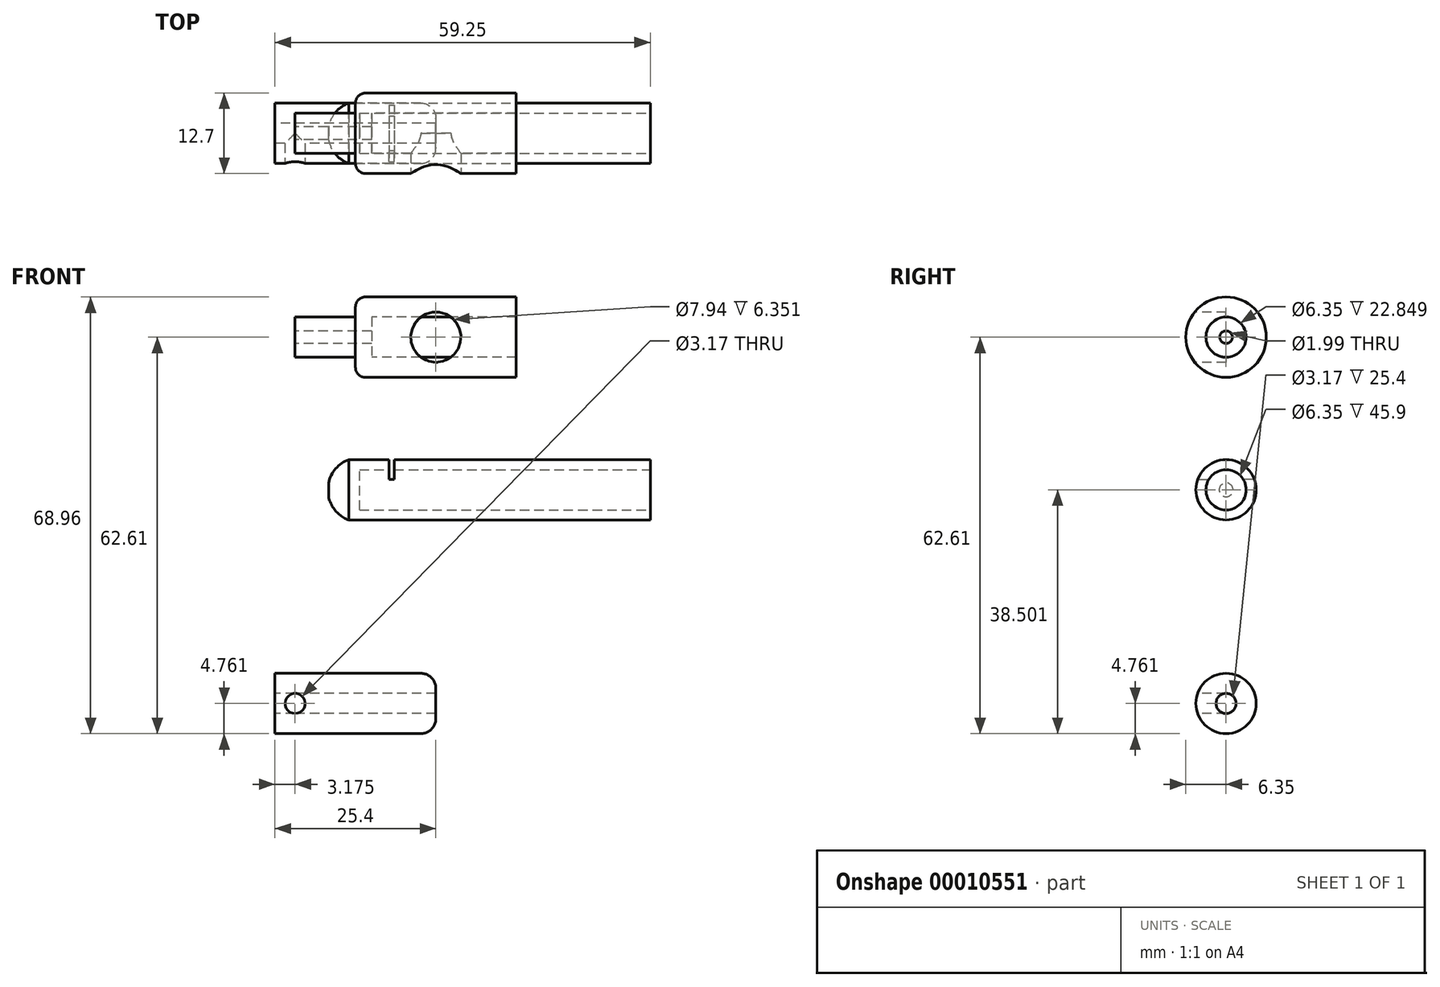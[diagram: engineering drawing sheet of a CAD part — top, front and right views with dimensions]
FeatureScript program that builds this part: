
annotation { "Feature Type Name" : "Feature", "Feature Type Description" : "" }
export const myFeature = defineFeature(function(context is Context, id is Id, definition is map)
    precondition{}
    {
        {
            var Q0;
            Q0=qCreatedBy(makeId("Front.planeOp"),FACE);
            var sketch = newSketch(context, id + "F0", { "sketchPlane" : qUnion([Q0])});
            skLineSegment(sketch, "E0.rect.bottom", {"start": v(12.7, -6.35) * mm, "end": v(-12.7, -6.35) * mm});
            skLineSegment(sketch, "E0.rect.top", {"start": v(12.7, 6.35) * mm, "end": v(-12.7, 6.35) * mm});
            skLineSegment(sketch, "E0.rect.left", {"start": v(12.7, -6.35) * mm, "end": v(12.7, 6.35) * mm});
            skLineSegment(sketch, "E0.rect.right", {"start": v(-12.7, -6.35) * mm, "end": v(-12.7, 6.35) * mm});
            skPoint(sketch, "E0.rect.middle", {"position": v(0, 0) * mm});
            skLineSegment(sketch, "E1.rect.bottom", {"start": v(-12.7, 3.18) * mm, "end": v(-22.23, 3.18) * mm});
            skLineSegment(sketch, "E1.rect.top", {"start": v(-12.7, -3.18) * mm, "end": v(-22.23, -3.17) * mm});
            skLineSegment(sketch, "E1.rect.left", {"start": v(-12.7, 3.18) * mm, "end": v(-12.7, -3.17) * mm});
            skLineSegment(sketch, "E1.rect.right", {"start": v(-22.23, 3.18) * mm, "end": v(-22.23, -3.17) * mm});
            skPoint(sketch, "E1.rect.middle", {"position": v(-17.46, 0) * mm});
            skCircle(sketch, "E2", {"center": v(0, 0) * mm, "radius": 3.97 * mm});
            skLineSegment(sketch, "E3.bottom", {"start": v(-16.95, -19.35) * mm, "end": v(33.85, -19.35) * mm});
            skLineSegment(sketch, "E3.top", {"start": v(-16.95, -28.87) * mm, "end": v(33.85, -28.87) * mm});
            skLineSegment(sketch, "E3.left", {"start": v(-16.95, -19.35) * mm, "end": v(-16.95, -28.87) * mm});
            skLineSegment(sketch, "E3.right", {"start": v(33.85, -19.35) * mm, "end": v(33.85, -28.87) * mm});
            skLineSegment(sketch, "E4", {"start": v(-13.77, -16.16) * mm, "end": v(-13.77, -32.25) * mm, "construction": true});
            skArc(sketch, "E5", {"start": v(-13.77, -19.35) * mm, "mid": v(-17.06, -24.1) * mm, "end": v(-13.77, -28.87) * mm});
            skLineSegment(sketch, "E6.rect.bottom", {"start": v(-12.05, -20.93) * mm, "end": v(79.75, -20.93) * mm});
            skLineSegment(sketch, "E6.rect.top", {"start": v(-12.05, -27.28) * mm, "end": v(79.75, -27.28) * mm});
            skLineSegment(sketch, "E6.rect.left", {"start": v(-12.05, -20.93) * mm, "end": v(-12.05, -27.28) * mm});
            skLineSegment(sketch, "E6.rect.right", {"start": v(79.75, -20.93) * mm, "end": v(79.75, -27.28) * mm});
            skPoint(sketch, "E6.rect.middle", {"position": v(33.85, -24.1) * mm});
            skLineSegment(sketch, "E7", {"start": v(33.85, -24.1) * mm, "end": v(-27.42, -24.1) * mm});
            skLineSegment(sketch, "E8.bottom", {"start": v(-7.42, -22.49) * mm, "end": v(-6.57, -22.49) * mm});
            skLineSegment(sketch, "E8.top", {"start": v(-7.42, -15.2) * mm, "end": v(-6.57, -15.2) * mm});
            skLineSegment(sketch, "E8.left", {"start": v(-7.42, -22.49) * mm, "end": v(-7.42, -15.2) * mm});
            skLineSegment(sketch, "E8.right", {"start": v(-6.57, -22.49) * mm, "end": v(-6.57, -15.2) * mm});
            skLineSegment(sketch, "E9", {"start": v(-25.32, 0) * mm, "end": v(20.75, 0) * mm});
            skLineSegment(sketch, "E10.bottom", {"start": v(-22.23, 0) * mm, "end": v(12.7, 0) * mm});
            skLineSegment(sketch, "E10.top", {"start": v(-22.23, 1) * mm, "end": v(12.7, 1) * mm});
            skLineSegment(sketch, "E10.left", {"start": v(-22.23, 0) * mm, "end": v(-22.23, 1) * mm});
            skLineSegment(sketch, "E10.right", {"start": v(12.7, 0) * mm, "end": v(12.7, 1) * mm});
            skLineSegment(sketch, "E11.bottom", {"start": v(-10.15, 0) * mm, "end": v(12.7, 0) * mm});
            skLineSegment(sketch, "E11.top", {"start": v(-10.15, 3.18) * mm, "end": v(12.7, 3.18) * mm});
            skLineSegment(sketch, "E11.left", {"start": v(-10.15, 0) * mm, "end": v(-10.15, 3.18) * mm});
            skLineSegment(sketch, "E11.right", {"start": v(12.7, 0) * mm, "end": v(12.7, 3.18) * mm});
            skLineSegment(sketch, "E12.rect.bottom", {"start": v(0, -56.26) * mm, "end": v(-25.4, -56.26) * mm});
            skLineSegment(sketch, "E12.rect.top", {"start": v(0, -53.09) * mm, "end": v(-25.4, -53.09) * mm});
            skLineSegment(sketch, "E12.rect.left", {"start": v(0, -56.26) * mm, "end": v(0, -53.09) * mm});
            skLineSegment(sketch, "E12.rect.right", {"start": v(-25.4, -56.26) * mm, "end": v(-25.4, -53.09) * mm});
            skPoint(sketch, "E12.rect.middle", {"position": v(-12.7, -54.67) * mm});
            skLineSegment(sketch, "E13.bottom", {"start": v(-25.4, -56.26) * mm, "end": v(0, -56.26) * mm});
            skLineSegment(sketch, "E13.top", {"start": v(-25.4, -57.85) * mm, "end": v(0, -57.85) * mm});
            skLineSegment(sketch, "E13.left", {"start": v(-25.4, -56.26) * mm, "end": v(-25.4, -57.85) * mm});
            skLineSegment(sketch, "E13.right", {"start": v(0, -56.26) * mm, "end": v(0, -57.85) * mm});
            skLineSegment(sketch, "E14", {"start": v(-22.23, -51.73) * mm, "end": v(-22.23, -59.92) * mm, "construction": true});
            skCircle(sketch, "E15", {"center": v(-22.23, -57.85) * mm, "radius": 0.43 * mm});
            skSolve(sketch);
        }
        {
            var Q0;
            {var subQ5=sQuery(id+"F0.wireOp",EDGE,"E3.right");var subQ10=sQuery(id+"F0.wireOp",EDGE,"E3.bottom");var subQ13=makeQuery(id+"F0.imprint","INTERSECT",VERTEX,{"derivedFrom":[subQ10,subQ5]});Q0=makeQuery(id+"F0.imprint","IMPRINT",FACE,{"disambiguationData":[TD([[makeQuery(id+"F0.imprint","IMPRINT",EDGE,{"disambiguationData":[TD([[subQ13,1.0]])],"derivedFrom":subQ10}),-1.0]])]});}
            var Q1;
            {var subQ3=sQuery(id+"F0.wireOp",EDGE,"E3.bottom");var subQ11=sQuery(id+"F0.wireOp",EDGE,"E5");var subQ13=makeQuery(id+"F0.imprint","INTERSECT",VERTEX,{"derivedFrom":[subQ3,subQ11]});Q1=makeQuery(id+"F0.imprint","IMPRINT",FACE,{"disambiguationData":[TD([[makeQuery(id+"F0.imprint","IMPRINT",EDGE,{"disambiguationData":[TD([[subQ13,-1.0]])],"derivedFrom":subQ3}),-1.0]])]});}
            var Q2;
            {var subQ3=sQuery(id+"F0.wireOp",EDGE,"E3.bottom");var subQ5=sQuery(id+"F0.wireOp",EDGE,"E8.left");var subQ7=makeQuery(id+"F0.imprint","INTERSECT",VERTEX,{"derivedFrom":[subQ3,subQ5]});Q2=makeQuery(id+"F0.imprint","IMPRINT",FACE,{"disambiguationData":[TD([[makeQuery(id+"F0.imprint","IMPRINT",EDGE,{"disambiguationData":[TD([[subQ7,-1.0]])],"derivedFrom":subQ3}),-1.0]])]});}
            var Q3;
            Q3=sQuery(id+"F0.wireOp",EDGE,"E7");
            revolve(context, id + "F1", {"entities" : qUnion([Q0, Q1, Q2]), "axis" : qUnion([Q3]), "revolveType" : RevolveType.FULL});
        }
        {
            var Q0;
            {var subQ5=sQuery(id+"F0.wireOp",EDGE,"E1.rect.bottom");Q0=makeQuery(id+"F0.imprint","IMPRINT",FACE,{"disambiguationData":[TD([[makeQuery(id+"F0.imprint","IMPRINT",EDGE,{"derivedFrom":subQ5}),1.0]])]});}
            var Q1;
            {var subQ14=sQuery(id+"F0.wireOp",EDGE,"E0.rect.top");Q1=makeQuery(id+"F0.imprint","IMPRINT",FACE,{"disambiguationData":[TD([[makeQuery(id+"F0.imprint","IMPRINT",EDGE,{"derivedFrom":subQ14}),1.0]])]});}
            var Q2;
            {var subQ0=sQuery(id+"F0.wireOp",EDGE,"E11.top");var subQ1=sQuery(id+"F0.wireOp",EDGE,"E2");var subQ3=makeQuery(id+"F0.imprint","INTERSECT",VERTEX,{"disambiguationData":[OD(0.0)],"derivedFrom":[subQ1,subQ0]});Q2=makeQuery(id+"F0.imprint","IMPRINT",FACE,{"disambiguationData":[TD([[makeQuery(id+"F0.imprint","IMPRINT",EDGE,{"disambiguationData":[TD([[subQ3,-1.0]])],"derivedFrom":subQ1}),1.0]])]});}
            var Q3;
            Q3=sQuery(id+"F0.wireOp",EDGE,"E9");
            revolve(context, id + "F2", {"entities" : qUnion([Q0, Q1, Q2]), "axis" : qUnion([Q3]), "revolveType" : RevolveType.FULL});
        }
        {
            var Q0;
            Q0=makeQuery(id+"F2.opRevolve","SWEPT_EDGE",EDGE,{"disambiguationData":[OSD([sQuery(id+"F0.wireOp",EDGE,"E0.rect.top"),sQuery(id+"F0.wireOp",EDGE,"E0.rect.right")])]});
            fillet(context, id + "F3", {"entities" : qUnion([Q0]), "radius" : 1.59 * mm, "tangentPropagation" : true, "allowEdgeOverflow" : false});
        }
        {
            var Q0;
            Q0=sQuery(id+"F0.wireOp",VERTEX,"E2.center");
            var Q1;
            Q1=makeQuery(id+"F2.opRevolve","SWEPT_BODY",BODY,{"disambiguationData":[OSD([sQuery(id+"F0.wireOp",EDGE,"E0.rect.top"),sQuery(id+"F0.wireOp",EDGE,"E0.rect.left"),sQuery(id+"F0.wireOp",EDGE,"E0.rect.right"),sQuery(id+"F0.wireOp",EDGE,"E1.rect.bottom"),sQuery(id+"F0.wireOp",EDGE,"E1.rect.right"),sQuery(id+"F0.wireOp",EDGE,"E10.top"),sQuery(id+"F0.wireOp",EDGE,"E11.top"),sQuery(id+"F0.wireOp",EDGE,"E11.left")])]});
            hole(context, id + "F4", {"style" : HoleStyle.SIMPLE, "holeDiameter" : 7.94 * mm, "endStyle" : HoleEndStyle.THROUGH, "oppositeDirection" : true, "locations" : qUnion([Q0]), "scope" : qUnion([Q1])});
        }
        {
            var Q0;
            Q0=qCreatedBy(makeId("Front.planeOp"),FACE);
            var sketch = newSketch(context, id + "F5", { "sketchPlane" : qUnion([Q0])});
            skLineSegment(sketch, "E16.0", {"start": v(-6.57, -22.49) * mm, "end": v(-6.57, -15.2) * mm});
            skLineSegment(sketch, "E16.1", {"start": v(-7.42, -22.49) * mm, "end": v(-7.42, -15.2) * mm});
            skLineSegment(sketch, "E16.2", {"start": v(-7.42, -15.2) * mm, "end": v(-6.57, -15.2) * mm});
            skLineSegment(sketch, "E16.3", {"start": v(-7.42, -22.49) * mm, "end": v(-6.57, -22.49) * mm});
            skSolve(sketch);
        }
        {
            var Q0;
            Q0=makeQuery(id+"F5.imprint","IMPRINT",FACE,{"disambiguationData":[TD([[makeQuery(id+"F5.imprint","IMPRINT",EDGE,{"derivedFrom":sQuery(id+"F5.wireOp",EDGE,"E16.0")}),1.0]])]});
            extrude(context, id + "F6", {"entities" : qUnion([Q0]), "operationType" : NewBodyOperationType.REMOVE, "oppositeDirection" : true, "depth" : 50.8 * mm});
        }
        {
            var Q0;
            Q0=makeQuery(id+"F0.imprint","IMPRINT",FACE,{"disambiguationData":[TD([[makeQuery(id+"F0.imprint","IMPRINT",EDGE,{"derivedFrom":sQuery(id+"F0.wireOp",EDGE,"E12.rect.top")}),1.0]])]});
            var Q1;
            Q1=sQuery(id+"F0.wireOp",EDGE,"E13.top");
            revolve(context, id + "F7", {"entities" : qUnion([Q0]), "axis" : qUnion([Q1]), "revolveType" : RevolveType.FULL});
        }
        {
            var Q0;
            Q0=sQuery(id+"F0.wireOp",VERTEX,"E15.center");
            var Q1;
            Q1=makeQuery(id+"F7.opRevolve","SWEPT_BODY",BODY,{"disambiguationData":[OSD([sQuery(id+"F0.wireOp",EDGE,"E12.rect.top"),sQuery(id+"F0.wireOp",EDGE,"E12.rect.left"),sQuery(id+"F0.wireOp",EDGE,"E12.rect.right"),sQuery(id+"F0.wireOp",EDGE,"E13.bottom")])]});
            hole(context, id + "F8", {"style" : HoleStyle.SIMPLE, "holeDiameter" : 3.17 * mm, "endStyle" : HoleEndStyle.THROUGH, "oppositeDirection" : true, "locations" : qUnion([Q0]), "scope" : qUnion([Q1])});
        }
        {
            var Q0;
            Q0=makeQuery(id+"F7.opRevolve","SWEPT_EDGE",EDGE,{"disambiguationData":[OSD([sQuery(id+"F0.wireOp",EDGE,"E12.rect.top"),sQuery(id+"F0.wireOp",EDGE,"E12.rect.left")])]});
            fillet(context, id + "F9", {"entities" : qUnion([Q0]), "radius" : 2.38 * mm, "tangentPropagation" : true, "allowEdgeOverflow" : false});
        }
        {
            var Q0;
            {var subQ3=sQuery(id+"F0.wireOp",EDGE,"E8.bottom");Q0=makeQuery(id+"F0.imprint","IMPRINT",FACE,{"disambiguationData":[TD([[makeQuery(id+"F0.imprint","IMPRINT",EDGE,{"derivedFrom":subQ3}),1.0]])]});}
            var Q1;
            {var subQ0=sQuery(id+"F0.wireOp",EDGE,"E8.left");var subQ3=sQuery(id+"F0.wireOp",EDGE,"E3.bottom");var subQ4=makeQuery(id+"F0.imprint","INTERSECT",VERTEX,{"derivedFrom":[subQ3,subQ0]});Q1=makeQuery(id+"F0.imprint","IMPRINT",FACE,{"disambiguationData":[TD([[makeQuery(id+"F0.imprint","IMPRINT",EDGE,{"disambiguationData":[TD([[subQ4,-1.0]])],"derivedFrom":subQ3}),-1.0]])]});}
            extrude(context, id + "F10", {"entities" : qUnion([Q0, Q1]), "operationType" : NewBodyOperationType.REMOVE, "depth" : 25.4 * mm});
        }
    });
